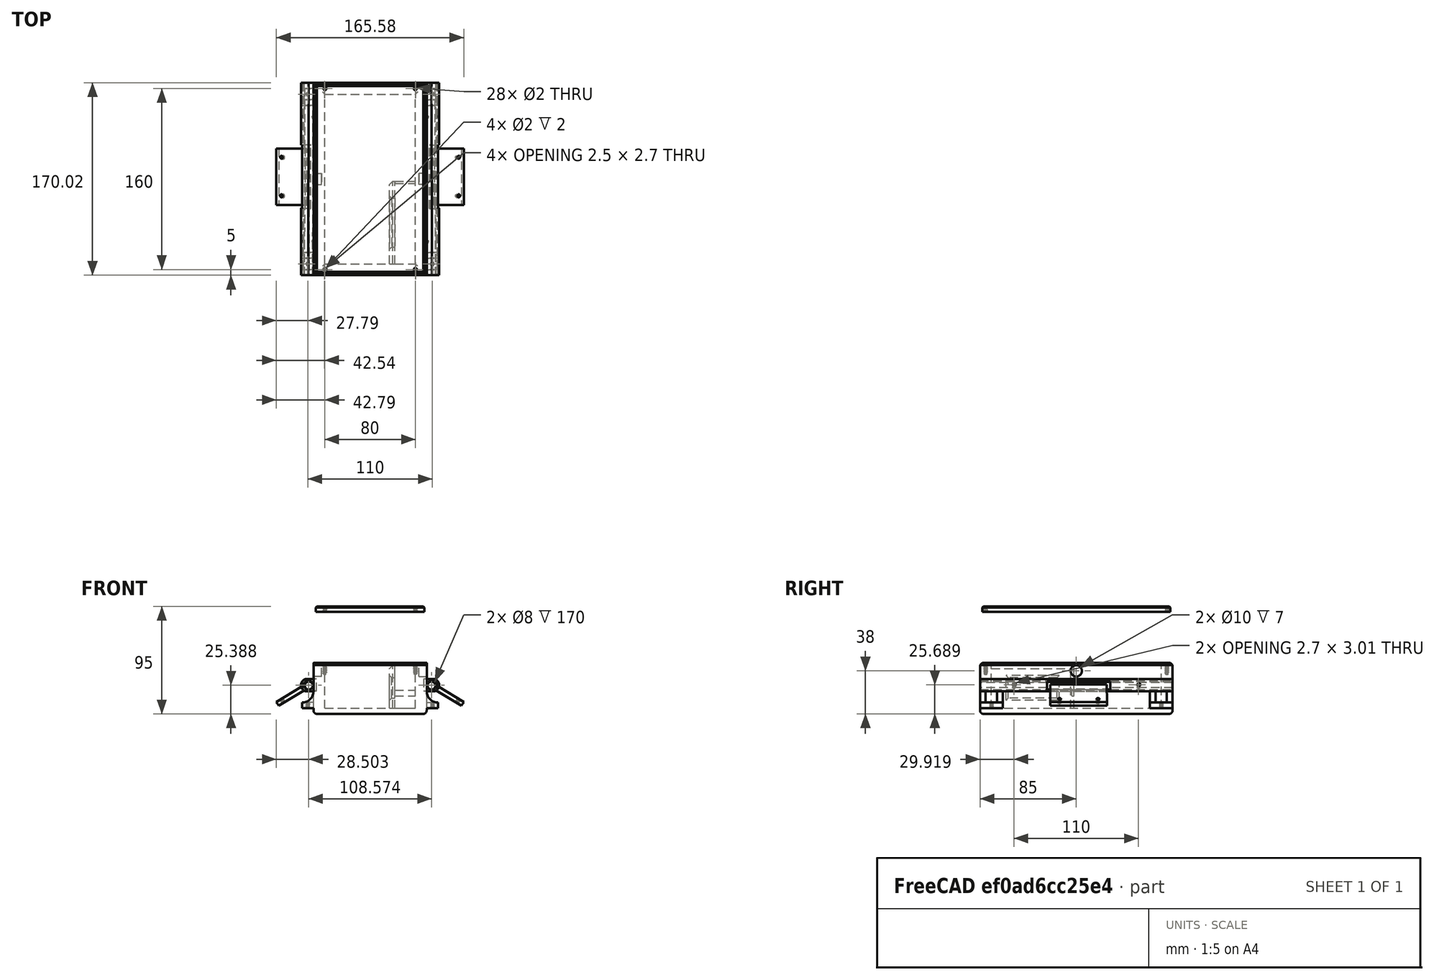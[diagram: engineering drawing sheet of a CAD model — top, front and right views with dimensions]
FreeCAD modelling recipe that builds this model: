
FCSTD DOCUMENT  (FreeCAD 0.21R33694 (Git))
Label: merged-carcasa
License: Creative Commons Attribution-NonCommercial-ShareAlike 4.0
LicenseURL: https://creativecommons.org/licenses/by-nc-sa/4.0/
objects: Part::Fuse×24, Part::Cut×12, Part::Mirroring×12, Part::Box×11, Part::Feature×8, Part::Cylinder×7, Part::Chamfer×4, Sketcher::SketchObject×3, Part::Extrusion×3, Part::Fillet×3, Part::Compound×2, App::FeaturePython×2, PartDesign::Body×1, Part::MultiFuse×1, Part::Refine×1
note: 92 computed .brp shape members not serialized (recipe doc carries the construction recipe); baked Part::Feature solids carry a one-line shape summary decoded from their .brp

FEATURE [Sketcher::SketchObject] Sketch  label="case-taladros"
  FullyConstrained = true
  MapMode = 5
  Support = -> [XY_Plane]
  sketch-geometry (8):
    g0: LineSegment StartX=-50 StartY=85 StartZ=0 EndX=50 EndY=85 EndZ=0
    g1: LineSegment StartX=50 StartY=85 StartZ=0 EndX=50 EndY=-85 EndZ=0
    g2: LineSegment StartX=50 StartY=-85 StartZ=0 EndX=-50 EndY=-85 EndZ=0
    g3: LineSegment StartX=-50 StartY=-85 StartZ=0 EndX=-50 EndY=85 EndZ=0
    g4: Circle CenterX=-40 CenterY=80 CenterZ=0 NormalX=0 NormalY=0 NormalZ=1 AngleXU=0 Radius=1.5
    g5: Circle CenterX=40 CenterY=80 CenterZ=0 NormalX=0 NormalY=0 NormalZ=1 AngleXU=0 Radius=1.5
    g6: Circle CenterX=40 CenterY=-80 CenterZ=0 NormalX=0 NormalY=0 NormalZ=1 AngleXU=0 Radius=1.5
    g7: Circle CenterX=-40 CenterY=-80 CenterZ=0 NormalX=0 NormalY=0 NormalZ=1 AngleXU=0 Radius=1.5
  constraints (19):
    c: Coincident(g0,g1)
    c: Coincident(g1,g2)
    c: Coincident(g2,g3)
    c: Coincident(g3,g0)
    c: Horizontal(g2)
    c: Vertical(g1)
    c: Symmetric(g0,g0,g-2)
    c: Symmetric(g2,g0,g-1)
    c: Equal(g4,g7)
    c: Equal(g7,g6)
    c: Equal(g6,g5)
    c: Symmetric(g7,g4,g-1)
    c: Symmetric(g4,g5,g-2)
    c: Symmetric(g6,g7,g-2)
    c: Diameter(g4) = 3
    c: DistanceY(g4,g0) = 5
    c: DistanceX(g0,g4) = 10
    c: DistanceY(g3,g3) = 170
    c: DistanceX(g0,g0) = 100
FEATURE [PartDesign::Body] Body  label="carcasa-boceto"
  Group = -> [Sketch]
  Origin = -> Origin
FEATURE [Part::Extrusion] Extrude  label="carcasa-extruida"
  Base = -> Sketch
  Dir = (0,0,1)
  DirMode = 2
  FaceMakerClass = Part::FaceMakerBullseye
  LengthFwd = 45
  LengthRev = 0
  Solid = true
  Symmetric = false
FEATURE [Part::Box] Box  label="llenado"
  AttacherType = Attacher::AttachEngine3D
  Height = 35
  Length = 100
  Placement = pos=(-50,-85,0) rot=(0,0,1;0rad)
  Width = 170
FEATURE [Part::Fuse] Fusion  label="carcasa-taladrada"
  Base = -> Extrude
  Refine = true
  Tool = -> Box
FEATURE [Part::Box] Box001  label="vaciado"
  AttacherType = Attacher::AttachEngine3D
  Height = 40
  Length = 80
  Placement = pos=(-40,-75,5) rot=(0,0,1;0rad)
  Width = 150
FEATURE [Part::Cut] Cut  label="carcasa-vaciada"
  Base = -> Fusion
  Refine = true
  Tool = -> Box001
FEATURE [Part::Fillet] Fillet
  Base = -> Cut
  Edges = 4 edges r=2: [Edge8,Edge9,Edge10,Edge11]
FEATURE [Part::Chamfer] Chamfer  label="carcasa001"
  Base = -> Fillet
  Edges = 4 edges r=2: [Edge5,Edge6,Edge7,Edge8]
FEATURE [Sketcher::SketchObject] Sketch008  label="tapa-taladros"
  FullyConstrained = true
  MapMode = 5
  sketch-geometry (8):
    g0: LineSegment StartX=-48 StartY=83 StartZ=0 EndX=48 EndY=83 EndZ=0
    g1: LineSegment StartX=48 StartY=83 StartZ=0 EndX=48 EndY=-83 EndZ=0
    g2: LineSegment StartX=48 StartY=-83 StartZ=0 EndX=-48 EndY=-83 EndZ=0
    g3: LineSegment StartX=-48 StartY=-83 StartZ=0 EndX=-48 EndY=83 EndZ=0
    g4: Circle CenterX=-40 CenterY=80 CenterZ=0 NormalX=0 NormalY=0 NormalZ=1 AngleXU=0 Radius=0.5
    g5: Circle CenterX=40 CenterY=80 CenterZ=0 NormalX=0 NormalY=0 NormalZ=1 AngleXU=0 Radius=0.5
    g6: Circle CenterX=40 CenterY=-80 CenterZ=0 NormalX=0 NormalY=0 NormalZ=1 AngleXU=0 Radius=0.5
    g7: Circle CenterX=-40 CenterY=-80 CenterZ=0 NormalX=0 NormalY=0 NormalZ=1 AngleXU=0 Radius=0.5
  constraints (19):
    c: Coincident(g0,g1)
    c: Coincident(g1,g2)
    c: Coincident(g2,g3)
    c: Coincident(g3,g0)
    c: Horizontal(g2)
    c: Vertical(g1)
    c: Symmetric(g0,g0,g-2)
    c: Symmetric(g2,g0,g-1)
    c: Equal(g4,g7)
    c: Equal(g7,g6)
    c: Equal(g6,g5)
    c: Symmetric(g7,g4,g-1)
    c: Symmetric(g4,g5,g-2)
    c: Symmetric(g6,g7,g-2)
    c: Diameter(g4) = 1
    c: DistanceY(g4,g0) = 3
    c: DistanceX(g0,g4) = 8
    c: DistanceY(g3,g3) = 166
    c: DistanceX(g0,g0) = 96
FEATURE [Part::Extrusion] Extrude002  label="tapa"
  Base = -> Sketch008
  Dir = (0,0,1)
  DirMode = 2
  FaceMakerClass = Part::FaceMakerBullseye
  LengthFwd = 5
  LengthRev = 0
  Placement = pos=(0,0,45) rot=(0,0,1;0rad)
  Solid = true
  Symmetric = false
FEATURE [Part::Chamfer] Chamfer001  label="tapa-case"
  Base = -> Extrude002
  Edges = 4 edges r=1: [Edge4,Edge7,Edge10,Edge12]
FEATURE [Part::Cylinder] Cylinder002  label="enbellezedor-cables"
  Angle = 360
  AttacherType = Attacher::AttachEngine3D
  FirstAngle = 0
  Height = 5
  Placement = pos=(45,0,39) rot=(0,1,0;1.5708rad)
  Radius = 6
  SecondAngle = 0
FEATURE [Part::Cylinder] Cylinder003  label="enbellezedor-cables2"
  Angle = 360
  AttacherType = Attacher::AttachEngine3D
  FirstAngle = 0
  Height = 5
  Placement = pos=(-50,0,39) rot=(0,1,0;1.5708rad)
  Radius = 6
  SecondAngle = 0
FEATURE [Part::Fuse] Fusion001013  label="enbellezedores-cables"
  Base = -> Cylinder002
  Refine = true
  Tool = -> Cylinder003
FEATURE [Part::Fuse] Fusion001014  label="carcasa002"
  Base = -> Chamfer
  Refine = true
  Tool = -> Fusion001013
FEATURE [Part::Cylinder] Cylinder004  label="agujero-cables"
  Angle = 360
  AttacherType = Attacher::AttachEngine3D
  FirstAngle = 0
  Height = 20
  Placement = pos=(43,0,38) rot=(0,1,0;1.5708rad)
  Radius = 5
  SecondAngle = 0
FEATURE [Part::Mirroring] Part__Mirroring007  label="agujero-cables (Mirror #8)"
  Base = (0,0,0)
  Normal = (1,0,0)
  Source = -> Cylinder004
FEATURE [Part::Fillet] Fillet002  label="carcasa003"
  Base = -> Fusion001014
  Edges = 4 edges r=3: [Edge49,Edge54,Edge63,Edge64]
FEATURE [Part::Cylinder] Cylinder005  label="rellenados"
  Angle = 360
  AttacherType = Attacher::AttachEngine3D
  FirstAngle = 0
  Height = 10
  Placement = pos=(-40,80,35) rot=(0,0,1;0rad)
  Radius = 1.5
  SecondAngle = 0
FEATURE [Part::Mirroring] Part__Mirroring008  label="rellenados (Mirror #9)"
  Base = (0,0,0)
  Normal = (1,0,0)
  Source = -> Cylinder005
FEATURE [Part::Fuse] Fusion001015  label="rellenados-1"
  Base = -> Cylinder005
  Refine = true
  Tool = -> Part__Mirroring008
FEATURE [Part::Cylinder] Cylinder006  label="rellenados001"
  Angle = 360
  AttacherType = Attacher::AttachEngine3D
  FirstAngle = 0
  Height = 10
  Placement = pos=(-40,80,35) rot=(0,0,1;0rad)
  Radius = 1.5
  SecondAngle = 0
FEATURE [Part::Mirroring] Part__Mirroring009  label="rellenados (Mirror #9)001"
  Base = (0,0,0)
  Normal = (1,0,0)
  Source = -> Cylinder006
FEATURE [Part::Fuse] Fusion001016  label="rellenados-2"
  Base = -> Cylinder006
  Placement = pos=(0,-160,0) rot=(0,0,1;0rad)
  Refine = true
  Tool = -> Part__Mirroring009
FEATURE [Part::Fuse] Fusion001017  label="rellenados002"
  Base = -> Fusion001015
  Refine = true
  Tool = -> Fusion001016
FEATURE [Part::Fuse] Fusion001018  label="carcasa004"
  Base = -> Fillet002
  Refine = true
  Tool = -> Fusion001017
FEATURE [Part::Feature] Fusion001001  label="Rosca macho002"
  Placement = pos=(40,-80,60) rot=(0,0,1;0rad)
  shape: bbox 3.919 x 4.387 x 44 mm, 35 faces (baked)
FEATURE [Part::Mirroring] Part__Mirroring004  label="Rosca macho002 (Mirror #5)"
  Base = (0,0,0)
  Normal = (1,0,0)
  Source = -> Fusion001001
FEATURE [Part::Mirroring] Part__Mirroring005  label="Rosca macho002 (Mirror #6)"
  Base = (0,0,0)
  Normal = (0,1,0)
  Source = -> Part__Mirroring004
FEATURE [Part::Mirroring] Part__Mirroring006  label="Rosca macho002 (Mirror #7)"
  Base = (0,0,0)
  Normal = (1,0,0)
  Source = -> Part__Mirroring005
FEATURE [Part::Fuse] Fusion001019
  Base = -> Part__Mirroring005
  Refine = true
  Tool = -> Part__Mirroring006
FEATURE [Part::Fuse] Fusion001020
  Base = -> Fusion001001
  Refine = true
  Tool = -> Part__Mirroring004
FEATURE [Part::Fuse] Fusion001021  label="roscas"
  Base = -> Fusion001019
  Placement = pos=(0,0,-24) rot=(0,0,1;0rad)
  Refine = true
  Tool = -> Fusion001020
FEATURE [Part::Feature] Fusion001022  label="Rosca macho010"
  Placement = pos=(40,-80,60) rot=(0,0,1;0rad)
  shape: bbox 3.919 x 4.387 x 44 mm, 35 faces (baked)
FEATURE [Part::Mirroring] Part__Mirroring010  label="Rosca macho002 (Mirror #5)001"
  Base = (0,0,0)
  Normal = (1,0,0)
  Source = -> Fusion001022
FEATURE [Part::Fuse] Fusion001024
  Base = -> Fusion001022
  Refine = true
  Tool = -> Part__Mirroring010
FEATURE [Part::Mirroring] Part__Mirroring011  label="Rosca macho002 (Mirror #6)001"
  Base = (0,0,0)
  Normal = (0,1,0)
  Source = -> Part__Mirroring010
FEATURE [Part::Mirroring] Part__Mirroring012  label="Rosca macho002 (Mirror #7)001"
  Base = (0,0,0)
  Normal = (1,0,0)
  Source = -> Part__Mirroring011
FEATURE [Part::Fuse] Fusion001023
  Base = -> Part__Mirroring011
  Refine = true
  Tool = -> Part__Mirroring012
FEATURE [Part::Fuse] Fusion001025  label="roscas001"
  Base = -> Fusion001023
  Placement = pos=(0,0,-24) rot=(0,0,1;0rad)
  Refine = true
  Tool = -> Fusion001024
FEATURE [Part::Cut] Cut025  label="tapa-shaded"
  Base = -> Chamfer001
  Placement = pos=(0,0,45) rot=(0,0,1;0rad)
  Refine = true
  Tool = -> Fusion001021
FEATURE [Part::Cut] Cut026  label="carcasa-roscada"
  Base = -> Fusion001018
  Refine = true
  Tool = -> Fusion001025
FEATURE [Part::Box] Box008  label="Cube"
  AttacherType = Attacher::AttachEngine3D
  Height = 5
  Length = 10
  Width = 20
FEATURE [Part::Box] Box009  label="Cube001"
  AttacherType = Attacher::AttachEngine3D
  Height = 50
  Length = 5
  Placement = pos=(-5,0,0) rot=(0,0,1;0rad)
  Width = 20
FEATURE [Part::Box] Box002  label="Cube002"
  AttacherType = Attacher::AttachEngine3D
  Height = 50
  Length = 5
  Placement = pos=(-5,0,0) rot=(0,0,1;0rad)
  Width = 20
FEATURE [Part::Box] Box003  label="Cube003"
  AttacherType = Attacher::AttachEngine3D
  Height = 20
  Length = 10
  Placement = pos=(0,5,5) rot=(0,0,1;0rad)
  Width = 10
FEATURE [Part::Cylinder] Cylinder
  Angle = 360
  AttacherType = Attacher::AttachEngine3D
  FirstAngle = 0
  Height = 6
  Placement = pos=(5,10,0) rot=(0,0,1;0rad)
  Radius = 0.5
  SecondAngle = 0
FEATURE [Part::Fuse] Fusion001026
  Base = -> Box008
  Refine = true
  Tool = -> Box009
FEATURE [Part::Fillet] Fillet003
  Base = -> Fusion001026
  Edges = 1 edges r=9.99: [Edge5]
FEATURE [Part::Cut] Cut027
  Base = -> Fillet003
  Refine = true
  Tool = -> Box002
FEATURE [Part::Cut] Cut001
  Base = -> Cut027
  Refine = true
  Tool = -> Box003
FEATURE [Part::Cut] Cut002  label="acople"
  Base = -> Cut001
  Refine = true
  Tool = -> Cylinder
FEATURE [Part::Feature] Fusion001027  label="Rosca macho011"
  Placement = pos=(5,10,-9) rot=(0,0,1;0rad)
  shape: bbox 3.919 x 4.387 x 44 mm, 35 faces (baked)
FEATURE [Part::Cut] Cut003  label="acople-roscado"
  Base = -> Cut002
  Placement = pos=(50,-85,5) rot=(0,0,1;0rad)
  Refine = true
  Tool = -> Fusion001027
FEATURE [Part::Mirroring] Part__Mirroring  label="acople-roscado (Mirror #11)"
  Base = (0,0,0)
  Normal = (1,0,0)
  Source = -> Cut003
FEATURE [Part::Fuse] Fusion001028
  Base = -> Cut003
  Refine = true
  Tool = -> Part__Mirroring
FEATURE [Part::Mirroring] Part__Mirroring013  label="Fusion001028 (Mirror #12)"
  Base = (0,0,0)
  Normal = (0,1,0)
  Source = -> Fusion001028
FEATURE [Part::Fuse] Fusion001029  label="acoples-flotador"
  Base = -> Fusion001028
  Refine = true
  Tool = -> Part__Mirroring013
FEATURE [Part::Fuse] Fusion001030  label="agujeros-cables"
  Base = -> Cylinder004
  Refine = true
  Tool = -> Part__Mirroring007
FEATURE [Part::Box] Box010  label="restriccion-lipo"
  AttacherType = Attacher::AttachEngine3D
  Height = 38
  Length = 5
  Placement = pos=(17,-75,5) rot=(0,0,1;0rad)
  Width = 73
FEATURE [Part::Box] Box011  label="restriccion-lipo001"
  AttacherType = Attacher::AttachEngine3D
  Height = 18
  Length = 7
  Placement = pos=(16,-60,14) rot=(0,0,1;0rad)
  Width = 43
FEATURE [Part::Cut] Cut028
  Base = -> Box010
  Refine = true
  Tool = -> Box011
FEATURE [Part::Chamfer] Chamfer002
  Base = -> Cut028
  Edges = 2 edges r=3: [Edge2,Edge4]
FEATURE [Part::Chamfer] Chamfer003
  Base = -> Chamfer002
  Edges = 4 edges r=2: [Edge5,Edge6,Edge7,Edge8]
FEATURE [Part::Box] Box012  label="Cube004"
  AttacherType = Attacher::AttachEngine3D
  Height = 5
  Length = 20
  Placement = pos=(20,-4,16) rot=(0,0,1;0rad)
  Width = 2
FEATURE [Part::Fuse] Fusion001032  label="rejillas-lipo"
  Base = -> Chamfer003
  Refine = true
  Tool = -> Box012
FEATURE [Part::Box] Box015  label="Cubo002"
  AttacherType = Attacher::AttachEngine3D
  Height = 4
  Length = 50
  Placement = pos=(-25,22,-7.5) rot=(0,0,1;0rad)
  Width = 30
FEATURE [Part::Box] Box016  label="cubo-corte"
  AttacherType = Attacher::AttachEngine3D
  Height = 20
  Length = 56
  Placement = pos=(-145,75,-20) rot=(0,0,1;0rad)
  Width = 16
FEATURE [Part::Cylinder] Cylinder007  label="Cilindro-movil"
  Angle = 360
  AttacherType = Attacher::AttachEngine3D
  FirstAngle = 0
  Height = 170
  Placement = pos=(-200,92,-6) rot=(0,1,0;1.5708rad)
  Radius = 3.5
  SecondAngle = 0
FEATURE [Part::Feature] Fusion001034  label="Rosca macho012"
  Placement = pos=(-17,27,-10) rot=(0,0,1;0rad)
  shape: bbox 3.919 x 4.387 x 44 mm, 35 faces (baked)
FEATURE [Part::Feature] Fusion001035  label="Rosca macho013"
  Placement = pos=(17,27,-10) rot=(0,0,1;0rad)
  shape: bbox 3.919 x 4.387 x 44 mm, 35 faces (baked)
FEATURE [Part::MultiFuse] Fusion001036
  Refine = true
  Shapes = -> [Fusion001034,Fusion001035]
FEATURE [Part::Cut] Cut030  label="Soporte_eje001"
  Base = -> Box015
  Placement = pos=(-117,38,0) rot=(0,0,1;0rad)
  Refine = true
  Tool = -> Fusion001036
FEATURE [Part::Feature] Fusion001037  label="Rosca macho014"
  Placement = pos=(-170,93.75,-8.78) rot=(0.819304,0.219813,-0.52955;0.936369rad)
  shape: bbox 4.221 x 33 x 32.52 mm, 35 faces (baked)
FEATURE [Part::Feature] Fusion001038  label="Rosca macho015"
  Placement = pos=(-60,93.75,-8.78) rot=(0.819304,0.219813,-0.52955;0.936369rad)
  shape: bbox 4.221 x 33 x 32.52 mm, 35 faces (baked)
FEATURE [Part::Fuse] Fusion001033  label="roscas002"
  Base = -> Fusion001037
  Refine = true
  Tool = -> Fusion001038
FEATURE [Part::Fuse] Fusion001039  label="cilindro-movil001"
  Base = -> Cut030
  Refine = true
  Tool = -> Cylinder007
FEATURE [Sketcher::SketchObject] Sketch009
  FullyConstrained = false
  MapMode = 5
  Placement = pos=(0,0,0) rot=(0.57735,0.57735,0.57735;2.0944rad)
  Support = -> [YZ_Plane004]
  sketch-geometry (9):
    g0: ArcOfCircle CenterX=0 CenterY=0 CenterZ=0 NormalX=0 NormalY=0 NormalZ=1 AngleXU=0 Radius=5.5 StartAngle=6.08579 EndAngle=9.70025
    g1: Circle CenterX=0 CenterY=-1.19343 CenterZ=0 NormalX=0 NormalY=0 NormalZ=1 AngleXU=0 Radius=4
    g2: LineSegment StartX=-2.36 StartY=4.37566 StartZ=0 EndX=2.36 EndY=4.37566 EndZ=0
    g3: LineSegment StartX=2.36 StartY=4.37566 StartZ=0 EndX=2.36 EndY=3.44566 EndZ=0
    g4: LineSegment StartX=2.36 StartY=3.44566 StartZ=0 EndX=-2.36 EndY=3.44566 EndZ=0
    g5: LineSegment StartX=-2.36 StartY=3.44566 StartZ=0 EndX=-2.36 EndY=4.37566 EndZ=0
    g6: LineSegment StartX=-5.29263 StartY=-1.49602 StartZ=0 EndX=-5.29263 EndY=-8 EndZ=0
    g7: LineSegment StartX=-5.29263 StartY=-8 StartZ=0 EndX=5.39319 EndY=-8 EndZ=0
    g8: LineSegment StartX=5.39319 StartY=-8 StartZ=0 EndX=5.39319 EndY=-1.07864 EndZ=0
  constraints (21):
    c: Coincident(g0,g-1)
    c: Coincident(g2,g3)
    c: Coincident(g3,g4)
    c: Coincident(g4,g5)
    c: Coincident(g5,g2)
    c: Horizontal(g4)
    c: Vertical(g3)
    c: Vertical(g5)
    c: Symmetric(g2,g2,g-2)
    c: PointOnObject(g1,g-2)
    c: Radius(g0) = 5.5
    c: Radius(g1) = 4
    c: DistanceY(g5,g5) = 0.93
    c: DistanceX(g2,g2) = 4.72
    c: Coincident(g6,g7)
    c: Coincident(g7,g8)
    c: Horizontal(g7)
    c: Vertical(g6)
    c: Vertical(g8)
    c: Coincident(g0,g8)
    c: Coincident(g6,g0)
FEATURE [Part::Extrusion] Extrude003  label="cilindro-fijo001"
  Base = -> Sketch009
  Dir = (1,-1e-16,1e-16)
  DirMode = 2
  FaceMakerClass = Part::FaceMakerBullseye
  LengthFwd = 170
  LengthRev = 0
  Placement = pos=(-200,91,-5) rot=(1,0,0;1.02974rad)
  Solid = true
  Symmetric = false
FEATURE [Part::Cut] Cut029
  Base = -> Extrude003
  Refine = true
  Tool = -> Fusion001033
FEATURE [Part::Cut] Cut031  label="fijacion-brazo"
  Base = -> Cut029
  Refine = true
  Tool = -> Box016
FEATURE [Part::Compound] Compound  label="brazo-mejorados"
  Links = -> [Cut031,Fusion001039]
  Placement = pos=(136,115,-16.54) rot=(0.259987,0.259987,0.929954;1.64236rad)
FEATURE [Part::Mirroring] Part__Mirroring014  label="brazo-mejorados (Mirror #13)"
  Base = (0,0,0)
  Normal = (1,0,0)
  Source = -> Compound
FEATURE [Part::Fuse] Fusion001040  label="brazos-v2"
  Base = -> Compound
  Placement = pos=(0,0.1,-1) rot=(0,0,1;3.14159rad)
  Refine = true
  Tool = -> Part__Mirroring014
FEATURE [Part::Fuse] Fusion001041
  Base = -> Cut026
  Refine = true
  Tool = -> Fusion001032
FEATURE [Part::Cut] Cut032  label="carcasa"
  Base = -> Fusion001041
  Refine = true
  Tool = -> Fusion001030
FEATURE [App::FeaturePython] planeCoincident_001  label="planeCoincident_001__acoples-flotador"  # a2plus constraint (typed FeaturePython)
  Object1 = Cut032
  Object2 = Fusion001029
  ParentTreeObject = -> Cut032
  SubElement1 = Face1
  SubElement2 = Face55
  Suppressed = false
  Type = plane
  directionConstraint = 0
  offset = 0
FEATURE [App::FeaturePython] planeCoincident_001_mirror  label="planeCoincident_001__carcasa"  # a2plus constraint (typed FeaturePython)
  Object1 = Cut032
  Object2 = Fusion001029
  ParentTreeObject = -> Fusion001029
  SubElement1 = Face1
  SubElement2 = Face55
  Suppressed = false
  Type = plane
  directionConstraint = 0
  offset = 0
FEATURE [Part::Fuse] Fusion001042
  Base = -> Fusion001040
  Refine = true
  Tool = -> Cut032
FEATURE [Part::Fuse] Fusion001043  label="caracasa-merged"
  Base = -> Fusion001029
  Refine = true
  Tool = -> Fusion001042
FEATURE [Part::Compound] Compound001  label="Compound-case"
  Links = -> [Fusion001043]
FEATURE [Part::Feature] Compound002  label="simple-compund"
  shape: bbox 165.6 x 170 x 47.45 mm, 315 faces, 3 solids (baked)
FEATURE [Part::Refine] Compound003  label="carcasa-shaded"
  Source = -> Compound002
